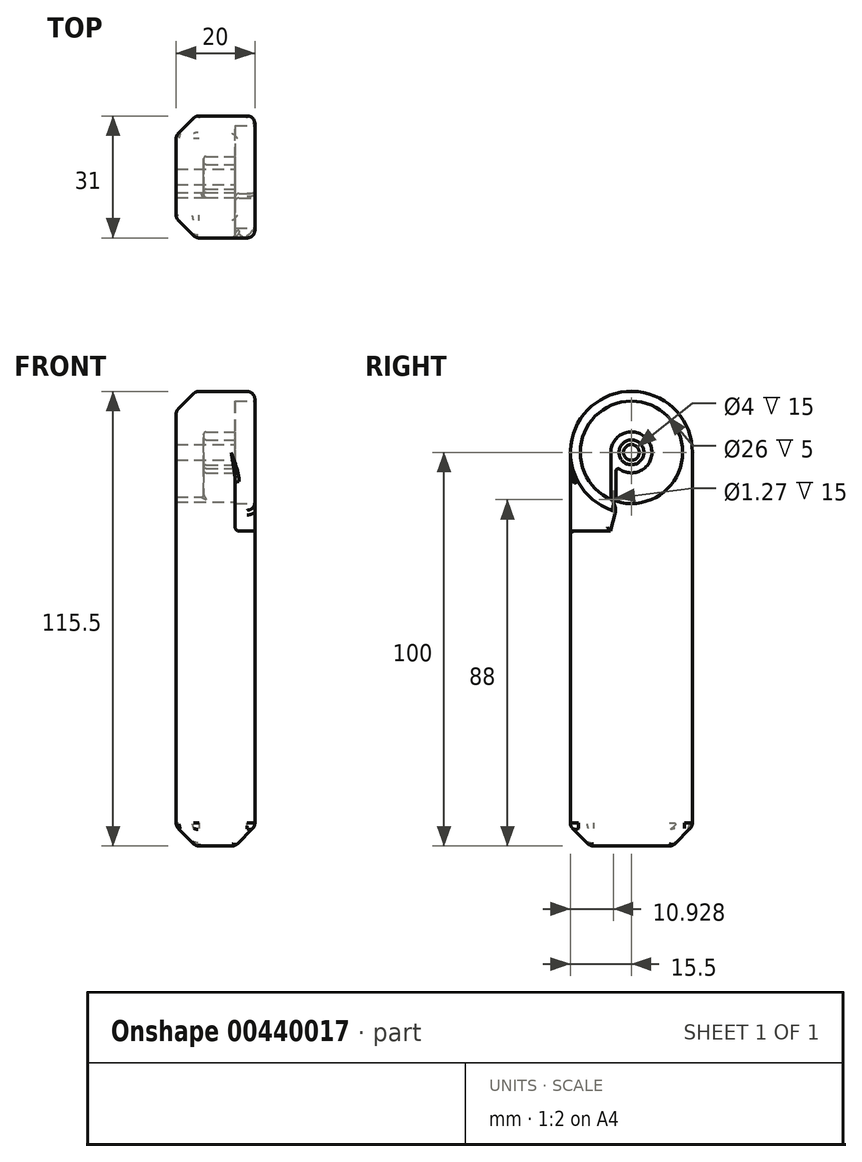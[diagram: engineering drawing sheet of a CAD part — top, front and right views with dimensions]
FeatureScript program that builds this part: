
annotation { "Feature Type Name" : "Feature", "Feature Type Description" : "" }
export const myFeature = defineFeature(function(context is Context, id is Id, definition is map)
    precondition{}
    {
        {
            var Q0;
            Q0=qCreatedBy(makeId("Right.planeOp"),FACE);
            var sketch = newSketch(context, id + "F0", { "sketchPlane" : qUnion([Q0])});
            skCircle(sketch, "E0", {"center": v(0, 0) * mm, "radius": 15.5 * mm});
            skCircle(sketch, "E1", {"center": v(0, 0) * mm, "radius": 2 * mm});
            skLineSegment(sketch, "E2.bottom", {"start": v(15.5, 0) * mm, "end": v(-15.5, 0) * mm});
            skLineSegment(sketch, "E2.top", {"start": v(15.5, -100) * mm, "end": v(-15.5, -100) * mm});
            skLineSegment(sketch, "E2.left", {"start": v(15.5, 0) * mm, "end": v(15.5, -100) * mm});
            skLineSegment(sketch, "E2.right", {"start": v(-15.5, 0) * mm, "end": v(-15.5, -100) * mm});
            skPoint(sketch, "E2.middle", {"position": v(0, -50) * mm});
            skSolve(sketch);
        }
        {
            var Q0;
            {var subQ0=sQuery(id+"F0.wireOp",EDGE,"E2.bottom");var subQ4=sQuery(id+"F0.wireOp",EDGE,"E1");var subQ5=makeQuery(id+"F0.imprint","INTERSECT",VERTEX,{"disambiguationData":[OD(0.0)],"derivedFrom":[subQ4,subQ0]});Q0=makeQuery(id+"F0.imprint","IMPRINT",FACE,{"disambiguationData":[TD([[makeQuery(id+"F0.imprint","IMPRINT",EDGE,{"disambiguationData":[TD([[subQ5,-1.0]])],"derivedFrom":subQ4}),-1.0]])]});}
            var Q1;
            {var subQ0=sQuery(id+"F0.wireOp",EDGE,"E2.bottom");var subQ4=sQuery(id+"F0.wireOp",EDGE,"E1");var subQ6=makeQuery(id+"F0.imprint","INTERSECT",VERTEX,{"disambiguationData":[OD(0.0)],"derivedFrom":[subQ4,subQ0]});Q1=makeQuery(id+"F0.imprint","IMPRINT",FACE,{"disambiguationData":[TD([[makeQuery(id+"F0.imprint","IMPRINT",EDGE,{"disambiguationData":[TD([[subQ6,1.0]])],"derivedFrom":subQ4}),-1.0]])]});}
            var Q2;
            Q2=makeQuery(id+"F0.imprint","IMPRINT",FACE,{"disambiguationData":[TD([[makeQuery(id+"F0.imprint","IMPRINT",EDGE,{"derivedFrom":sQuery(id+"F0.wireOp",EDGE,"E2.top")}),-1.0]])]});
            extrude(context, id + "F1", {"entities" : qUnion([Q0, Q1, Q2]), "oppositeDirection" : true, "depth" : 20 * mm, "offsetDistance" : 25 * mm});
        }
        {
            var Q0;
            Q0=makeQuery(id+"F1.opExtrude","CAP_FACE",FACE,{"disambiguationData":[OSD([sQuery(id+"F0.wireOp",EDGE,"E0"),sQuery(id+"F0.wireOp",EDGE,"E1"),sQuery(id+"F0.wireOp",EDGE,"E2.top"),sQuery(id+"F0.wireOp",EDGE,"E2.left"),sQuery(id+"F0.wireOp",EDGE,"E2.right")])],"isStart":true});
            var sketch = newSketch(context, id + "F2", { "sketchPlane" : qUnion([Q0])});
            skArc(sketch, "E3.0", {"start": v(15.5, 0) * mm, "mid": v(0, 15.5) * mm, "end": v(-15.5, 0) * mm});
            skCircle(sketch, "E4", {"center": v(0, 0) * mm, "radius": 15.5 * mm});
            skCircle(sketch, "E5.0", {"center": v(0, 0) * mm, "radius": 13 * mm});
            skLineSegment(sketch, "E6", {"start": v(0, 0) * mm, "end": v(-15.5, 0) * mm, "construction": true});
            skLineSegment(sketch, "E7", {"start": v(0, 0) * mm, "end": v(2.7, 15.26) * mm});
            skLineSegment(sketch, "E8", {"start": v(0, 0) * mm, "end": v(-4.01, -14.97) * mm});
            skLineSegment(sketch, "E9.0", {"start": v(-15.5, 0) * mm, "end": v(-15.5, -100) * mm});
            skLineSegment(sketch, "E10", {"start": v(-4.01, -14.97) * mm, "end": v(-5.36, -20) * mm});
            skLineSegment(sketch, "E11", {"start": v(-5.36, -20) * mm, "end": v(-15.5, -20) * mm});
            skSolve(sketch);
        }
        {
            var Q0;
            {var subQ1=sQuery(id+"F2.wireOp",EDGE,"E4");var subQ7=makeQuery(id+"F2.imprint","INTERSECT",VERTEX,{"derivedFrom":[subQ1,sQuery(id+"F2.wireOp",EDGE,"E9.0")]});Q0=makeQuery(id+"F2.imprint","IMPRINT",FACE,{"disambiguationData":[TD([[makeQuery(id+"F2.imprint","IMPRINT",EDGE,{"disambiguationData":[TD([[subQ7,1.0]])],"derivedFrom":subQ1}),1.0]])]});}
            var Q1;
            {var subQ0=sQuery(id+"F2.wireOp",EDGE,"E7");var subQ1=sQuery(id+"F2.wireOp",EDGE,"E5.0");var subQ2=makeQuery(id+"F2.imprint","INTERSECT",VERTEX,{"derivedFrom":[subQ1,subQ0]});Q1=makeQuery(id+"F2.imprint","IMPRINT",FACE,{"disambiguationData":[TD([[makeQuery(id+"F2.imprint","IMPRINT",EDGE,{"disambiguationData":[TD([[subQ2,-1.0]])],"derivedFrom":subQ1}),1.0]])]});}
            var Q2;
            {var subQ3=sQuery(id+"F2.wireOp",EDGE,"3M8qVWLi-stua-JPsy-CJId-azj3WznVmQZa");Q2=makeQuery(id+"F2.imprint","IMPRINT",FACE,{"disambiguationData":[TD([[makeQuery(id+"F2.imprint","IMPRINT",EDGE,{"derivedFrom":subQ3}),-1.0]])]});}
            var Q3;
            {var subQ0=sQuery(id+"F2.wireOp",EDGE,"E7");var subQ1=sQuery(id+"F2.wireOp",EDGE,"E5.0");var subQ2=makeQuery(id+"F2.imprint","INTERSECT",VERTEX,{"derivedFrom":[subQ1,subQ0]});Q3=makeQuery(id+"F2.imprint","IMPRINT",FACE,{"disambiguationData":[TD([[makeQuery(id+"F2.imprint","IMPRINT",EDGE,{"disambiguationData":[TD([[subQ2,1.0]])],"derivedFrom":subQ1}),1.0]])]});}
            var Q4;
            {var subQ3=sQuery(id+"F2.wireOp",EDGE,"E10");Q4=makeQuery(id+"F2.imprint","IMPRINT",FACE,{"disambiguationData":[TD([[makeQuery(id+"F2.imprint","IMPRINT",EDGE,{"derivedFrom":subQ3}),-1.0]])]});}
            extrude(context, id + "F3", {"entities" : qUnion([Q0, Q1, Q2, Q3, Q4]), "operationType" : NewBodyOperationType.REMOVE, "oppositeDirection" : true, "depth" : 5 * mm, "offsetDistance" : 25 * mm});
        }
        {
            var Q0;
            Q0=makeQuery(id+"F3.boolean.opBoolean","COPY",FACE,{"derivedFrom":makeQuery(id+"F3.opExtrude","CAP_FACE",FACE,{"disambiguationData":[OSD([sQuery(id+"F0.wireOp",EDGE,"E1"),sQuery(id+"F2.wireOp",EDGE,"E4"),sQuery(id+"F2.wireOp",EDGE,"E5.0"),sQuery(id+"F2.wireOp",EDGE,"E7"),sQuery(id+"F2.wireOp",EDGE,"E8"),sQuery(id+"F2.wireOp",EDGE,"E9.0"),sQuery(id+"F2.wireOp",EDGE,"E10"),sQuery(id+"F2.wireOp",EDGE,"E11")])],"isStart":false})});
            var sketch = newSketch(context, id + "F4", { "sketchPlane" : qUnion([Q0])});
            skCircle(sketch, "E12", {"center": v(0, 0) * mm, "radius": 3.15 * mm});
            skCircle(sketch, "E13", {"center": v(0, 0) * mm, "radius": 5.2 * mm});
            skLineSegment(sketch, "E14", {"start": v(-5.2, 0) * mm, "end": v(-5.2, -12) * mm});
            skLineSegment(sketch, "E15", {"start": v(-5.2, -12) * mm, "end": v(-3.94, -12) * mm});
            skLineSegment(sketch, "E16", {"start": v(-3.94, -12) * mm, "end": v(-3.94, -3.4) * mm});
            skCircle(sketch, "E17", {"center": v(-4.57, -12) * mm, "radius": 0.63 * mm});
            skSolve(sketch);
        }
        {
            var Q0;
            Q0=makeQuery(id+"F4.imprint","IMPRINT",FACE,{"disambiguationData":[TD([[makeQuery(id+"F4.imprint","IMPRINT",EDGE,{"derivedFrom":sQuery(id+"F4.wireOp",EDGE,"E12")}),-1.0]])]});
            var Q1;
            {var subQ0=sQuery(id+"F4.wireOp",EDGE,"E14");Q1=makeQuery(id+"F4.imprint","IMPRINT",FACE,{"disambiguationData":[TD([[makeQuery(id+"F4.imprint","IMPRINT",EDGE,{"derivedFrom":subQ0}),1.0]])]});}
            var Q2;
            {var subQ0=sQuery(id+"F4.wireOp",EDGE,"E15");Q2=makeQuery(id+"F4.imprint","IMPRINT",FACE,{"disambiguationData":[TD([[makeQuery(id+"F4.imprint","IMPRINT",EDGE,{"derivedFrom":subQ0}),-1.0]])]});}
            var Q3;
            {var subQ0=sQuery(id+"F4.wireOp",EDGE,"E15");Q3=makeQuery(id+"F4.imprint","IMPRINT",FACE,{"disambiguationData":[TD([[makeQuery(id+"F4.imprint","IMPRINT",EDGE,{"derivedFrom":subQ0}),1.0]])]});}
            extrude(context, id + "F5", {"entities" : qUnion([Q0, Q1, Q2, Q3]), "operationType" : NewBodyOperationType.REMOVE, "oppositeDirection" : true, "depth" : 8 * mm, "offsetDistance" : 25 * mm});
        }
        {
            var Q0;
            {var subQ0=sQuery(id+"F4.wireOp",EDGE,"E15");Q0=makeQuery(id+"F4.imprint","IMPRINT",FACE,{"disambiguationData":[TD([[makeQuery(id+"F4.imprint","IMPRINT",EDGE,{"derivedFrom":subQ0}),-1.0]])]});}
            var Q1;
            {var subQ0=sQuery(id+"F4.wireOp",EDGE,"E15");Q1=makeQuery(id+"F4.imprint","IMPRINT",FACE,{"disambiguationData":[TD([[makeQuery(id+"F4.imprint","IMPRINT",EDGE,{"derivedFrom":subQ0}),1.0]])]});}
            extrude(context, id + "F6", {"entities" : qUnion([Q0, Q1]), "operationType" : NewBodyOperationType.REMOVE, "endBound" : BoundingType.THROUGH_ALL, "oppositeDirection" : true, "depth" : 25 * mm, "offsetDistance" : 25 * mm});
        }
        {
            var Q0;
            Q0=makeQuery(id+"F5.boolean.opBoolean","COPY",FACE,{"derivedFrom":makeQuery(id+"F5.opExtrude","CAP_FACE",FACE,{"disambiguationData":[OSD([sQuery(id+"F4.wireOp",EDGE,"E12"),sQuery(id+"F4.wireOp",EDGE,"E13"),sQuery(id+"F4.wireOp",EDGE,"E14"),sQuery(id+"F4.wireOp",EDGE,"E16"),sQuery(id+"F4.wireOp",EDGE,"E17")])],"isStart":false})});
            var Q1;
            Q1=makeQuery(id+"F5.boolean.opBoolean","COPY",EDGE,{"derivedFrom":makeQuery(id+"F5.opExtrude","SWEPT_EDGE",EDGE,{"disambiguationData":[OSD([sQuery(id+"F4.wireOp",EDGE,"E13"),sQuery(id+"F4.wireOp",EDGE,"E16")])]})});
            var Q2;
            Q2=makeQuery(id+"F5.boolean.opBoolean","COPY",EDGE,{"derivedFrom":makeQuery(id+"F5.opExtrude","CAP_EDGE",EDGE,{"disambiguationData":[OSD([sQuery(id+"F4.wireOp",EDGE,"E13")])],"isStart":true})});
            var Q3;
            Q3=makeQuery(id+"F3.boolean.opBoolean","COPY",EDGE,{"derivedFrom":makeQuery(id+"F3.opExtrude","CAP_EDGE",EDGE,{"disambiguationData":[OSD([sQuery(id+"F0.wireOp",EDGE,"E1")])],"isStart":false})});
            fillet(context, id + "F7", {"entities" : qUnion([Q0, Q1, Q2, Q3]), "radius" : 0.6 * mm, "tangentPropagation" : true, "allowEdgeOverflow" : false});
        }
        {
            var Q0;
            Q0=makeQuery(id+"F1.opExtrude","CAP_EDGE",EDGE,{"disambiguationData":[OSD([sQuery(id+"F0.wireOp",EDGE,"E0")])],"isStart":false});
            var Q1;
            Q1=makeQuery(id+"F1.opExtrude","CAP_EDGE",EDGE,{"disambiguationData":[OSD([sQuery(id+"F0.wireOp",EDGE,"E2.top")])],"isStart":false});
            var Q2;
            Q2=makeQuery(id+"F1.opExtrude","SWEPT_EDGE",EDGE,{"disambiguationData":[OSD([sQuery(id+"F0.wireOp",EDGE,"E2.top"),sQuery(id+"F0.wireOp",EDGE,"E2.right")])]});
            var Q3;
            Q3=makeQuery(id+"F1.opExtrude","SWEPT_EDGE",EDGE,{"disambiguationData":[OSD([sQuery(id+"F0.wireOp",EDGE,"E2.top"),sQuery(id+"F0.wireOp",EDGE,"E2.left")])]});
            var Q4;
            Q4=makeQuery(id+"F1.opExtrude","CAP_EDGE",EDGE,{"disambiguationData":[OSD([sQuery(id+"F0.wireOp",EDGE,"E2.top")])],"isStart":true});
            chamfer(context, id + "F8", {"entities" : qUnion([Q0, Q1, Q2, Q3, Q4]), "width" : 5 * mm, "tangentPropagation" : true});
        }
        {
            var Q0;
            {var subQ0=sQuery(id+"F0.wireOp",EDGE,"E2.right");Q0=makeQuery(id+"F8.opChamfer","BLEND_EDGE",EDGE,{"blendedFrom":[makeQuery(id+"F1.opExtrude","CAP_EDGE",EDGE,{"disambiguationData":[OSD([subQ0])],"isStart":false}),makeQuery(id+"F1.opExtrude","CAP_FACE",FACE,{"disambiguationData":[OSD([sQuery(id+"F0.wireOp",EDGE,"E0"),sQuery(id+"F0.wireOp",EDGE,"E1"),sQuery(id+"F0.wireOp",EDGE,"E2.top"),sQuery(id+"F0.wireOp",EDGE,"E2.left"),subQ0])],"isStart":false})],"blendedInto":[makeQuery(id+"F1.opExtrude","CAP_FACE",FACE,{"disambiguationData":[OSD([sQuery(id+"F0.wireOp",EDGE,"E0"),sQuery(id+"F0.wireOp",EDGE,"E1"),sQuery(id+"F0.wireOp",EDGE,"E2.top"),sQuery(id+"F0.wireOp",EDGE,"E2.left"),subQ0])],"isStart":false})]});}
            var Q1;
            {var subQ0=sQuery(id+"F0.wireOp",EDGE,"E2.top");Q1=makeQuery(id+"F8.opChamfer","BLEND_EDGE",EDGE,{"blendedFrom":[makeQuery(id+"F1.opExtrude","CAP_EDGE",EDGE,{"disambiguationData":[OSD([subQ0])],"isStart":false}),makeQuery(id+"F1.opExtrude","CAP_FACE",FACE,{"disambiguationData":[OSD([sQuery(id+"F0.wireOp",EDGE,"E0"),sQuery(id+"F0.wireOp",EDGE,"E1"),subQ0,sQuery(id+"F0.wireOp",EDGE,"E2.left"),sQuery(id+"F0.wireOp",EDGE,"E2.right")])],"isStart":false})],"blendedInto":[makeQuery(id+"F1.opExtrude","CAP_FACE",FACE,{"disambiguationData":[OSD([sQuery(id+"F0.wireOp",EDGE,"E0"),sQuery(id+"F0.wireOp",EDGE,"E1"),subQ0,sQuery(id+"F0.wireOp",EDGE,"E2.left"),sQuery(id+"F0.wireOp",EDGE,"E2.right")])],"isStart":false})]});}
            var Q2;
            {var subQ0=sQuery(id+"F0.wireOp",EDGE,"E2.right");var subQ1=sQuery(id+"F0.wireOp",EDGE,"E2.top");Q2=makeQuery(id+"F8.opChamfer","BLEND_EDGE",EDGE,{"blendedFrom":[makeQuery(id+"F1.opExtrude","CAP_VERTEX",VERTEX,{"disambiguationData":[OSD([subQ1,subQ0])],"isStart":false}),makeQuery(id+"F1.opExtrude","SWEPT_EDGE",EDGE,{"disambiguationData":[OSD([subQ1,subQ0])]})],"blendedInto":[]});}
            var Q3;
            {var subQ0=sQuery(id+"F0.wireOp",EDGE,"E2.right");var subQ1=sQuery(id+"F0.wireOp",EDGE,"E2.top");Q3=makeQuery(id+"F8.opChamfer","BLEND_FACE",FACE,{"disambiguationData":[OSD([subQ1,subQ0]),TDD([makeQuery(id+"F1.opExtrude","CAP_VERTEX",VERTEX,{"disambiguationData":[OSD([subQ1,subQ0])],"isStart":false})])]});}
            var Q4;
            {var subQ0=sQuery(id+"F0.wireOp",EDGE,"E2.top");Q4=makeQuery(id+"F8.opChamfer","BLEND_EDGE",EDGE,{"blendedFrom":[makeQuery(id+"F1.opExtrude","CAP_EDGE",EDGE,{"disambiguationData":[OSD([subQ0])],"isStart":false}),makeQuery(id+"F1.opExtrude","SWEPT_FACE",FACE,{"disambiguationData":[OSD([subQ0])]})],"blendedInto":[makeQuery(id+"F1.opExtrude","SWEPT_FACE",FACE,{"disambiguationData":[OSD([subQ0])]})]});}
            var Q5;
            {var subQ0=sQuery(id+"F0.wireOp",EDGE,"E2.top");Q5=makeQuery(id+"F8.opChamfer","BLEND_EDGE",EDGE,{"blendedFrom":[makeQuery(id+"F1.opExtrude","SWEPT_EDGE",EDGE,{"disambiguationData":[OSD([subQ0,sQuery(id+"F0.wireOp",EDGE,"E2.right")])]}),makeQuery(id+"F1.opExtrude","SWEPT_FACE",FACE,{"disambiguationData":[OSD([subQ0])]})],"blendedInto":[makeQuery(id+"F1.opExtrude","SWEPT_FACE",FACE,{"disambiguationData":[OSD([subQ0])]})]});}
            var Q6;
            {var subQ0=sQuery(id+"F0.wireOp",EDGE,"E2.right");Q6=makeQuery(id+"F8.opChamfer","BLEND_EDGE",EDGE,{"blendedFrom":[makeQuery(id+"F1.opExtrude","SWEPT_EDGE",EDGE,{"disambiguationData":[OSD([sQuery(id+"F0.wireOp",EDGE,"E2.top"),subQ0])]}),makeQuery(id+"F1.opExtrude","SWEPT_FACE",FACE,{"disambiguationData":[OSD([subQ0])]})],"blendedInto":[makeQuery(id+"F1.opExtrude","SWEPT_FACE",FACE,{"disambiguationData":[OSD([subQ0])]})]});}
            var Q7;
            {var subQ0=sQuery(id+"F0.wireOp",EDGE,"E2.right");Q7=makeQuery(id+"F8.opChamfer","BLEND_EDGE",EDGE,{"blendedFrom":[makeQuery(id+"F1.opExtrude","CAP_EDGE",EDGE,{"disambiguationData":[OSD([subQ0])],"isStart":false}),makeQuery(id+"F1.opExtrude","SWEPT_FACE",FACE,{"disambiguationData":[OSD([subQ0])]})],"blendedInto":[makeQuery(id+"F1.opExtrude","SWEPT_FACE",FACE,{"disambiguationData":[OSD([subQ0])]})]});}
            var Q8;
            {var subQ0=sQuery(id+"F0.wireOp",EDGE,"E2.top");Q8=makeQuery(id+"F8.opChamfer","BLEND_EDGE",EDGE,{"blendedFrom":[makeQuery(id+"F1.opExtrude","CAP_VERTEX",VERTEX,{"disambiguationData":[OSD([subQ0,sQuery(id+"F0.wireOp",EDGE,"E2.left")])],"isStart":false}),makeQuery(id+"F1.opExtrude","CAP_EDGE",EDGE,{"disambiguationData":[OSD([subQ0])],"isStart":false})],"blendedInto":[]});}
            var Q9;
            {var subQ0=sQuery(id+"F0.wireOp",EDGE,"E2.left");Q9=makeQuery(id+"F8.opChamfer","BLEND_EDGE",EDGE,{"blendedFrom":[makeQuery(id+"F1.opExtrude","CAP_VERTEX",VERTEX,{"disambiguationData":[OSD([sQuery(id+"F0.wireOp",EDGE,"E2.top"),subQ0])],"isStart":false}),makeQuery(id+"F1.opExtrude","CAP_EDGE",EDGE,{"disambiguationData":[OSD([subQ0])],"isStart":false})],"blendedInto":[]});}
            var Q10;
            {var subQ0=sQuery(id+"F0.wireOp",EDGE,"E2.left");var subQ1=sQuery(id+"F0.wireOp",EDGE,"E2.top");Q10=makeQuery(id+"F8.opChamfer","BLEND_EDGE",EDGE,{"blendedFrom":[makeQuery(id+"F1.opExtrude","CAP_VERTEX",VERTEX,{"disambiguationData":[OSD([subQ1,subQ0])],"isStart":false}),makeQuery(id+"F1.opExtrude","SWEPT_EDGE",EDGE,{"disambiguationData":[OSD([subQ1,subQ0])]})],"blendedInto":[]});}
            var Q11;
            {var subQ0=sQuery(id+"F0.wireOp",EDGE,"E2.left");Q11=makeQuery(id+"F8.opChamfer","BLEND_EDGE",EDGE,{"blendedFrom":[makeQuery(id+"F1.opExtrude","SWEPT_EDGE",EDGE,{"disambiguationData":[OSD([sQuery(id+"F0.wireOp",EDGE,"E2.top"),subQ0])]}),makeQuery(id+"F1.opExtrude","SWEPT_FACE",FACE,{"disambiguationData":[OSD([subQ0])]})],"blendedInto":[makeQuery(id+"F1.opExtrude","SWEPT_FACE",FACE,{"disambiguationData":[OSD([subQ0])]})]});}
            var Q12;
            {var subQ0=sQuery(id+"F0.wireOp",EDGE,"E2.top");Q12=makeQuery(id+"F8.opChamfer","BLEND_EDGE",EDGE,{"blendedFrom":[makeQuery(id+"F1.opExtrude","SWEPT_EDGE",EDGE,{"disambiguationData":[OSD([subQ0,sQuery(id+"F0.wireOp",EDGE,"E2.left")])]}),makeQuery(id+"F1.opExtrude","SWEPT_FACE",FACE,{"disambiguationData":[OSD([subQ0])]})],"blendedInto":[makeQuery(id+"F1.opExtrude","SWEPT_FACE",FACE,{"disambiguationData":[OSD([subQ0])]})]});}
            var Q13;
            {var subQ0=sQuery(id+"F0.wireOp",EDGE,"E2.top");Q13=makeQuery(id+"F8.opChamfer","BLEND_EDGE",EDGE,{"blendedFrom":[makeQuery(id+"F1.opExtrude","SWEPT_EDGE",EDGE,{"disambiguationData":[OSD([subQ0,sQuery(id+"F0.wireOp",EDGE,"E2.right")])]}),makeQuery(id+"F1.opExtrude","CAP_EDGE",EDGE,{"disambiguationData":[OSD([subQ0])],"isStart":true})],"blendedInto":[]});}
            var Q14;
            {var subQ0=sQuery(id+"F0.wireOp",EDGE,"E2.top");Q14=makeQuery(id+"F8.opChamfer","BLEND_EDGE",EDGE,{"blendedFrom":[makeQuery(id+"F1.opExtrude","CAP_EDGE",EDGE,{"disambiguationData":[OSD([subQ0])],"isStart":true}),makeQuery(id+"F1.opExtrude","SWEPT_FACE",FACE,{"disambiguationData":[OSD([subQ0])]})],"blendedInto":[makeQuery(id+"F1.opExtrude","SWEPT_FACE",FACE,{"disambiguationData":[OSD([subQ0])]})]});}
            var Q15;
            {var subQ0=sQuery(id+"F0.wireOp",EDGE,"E2.top");Q15=makeQuery(id+"F8.opChamfer","BLEND_EDGE",EDGE,{"blendedFrom":[makeQuery(id+"F1.opExtrude","CAP_EDGE",EDGE,{"disambiguationData":[OSD([subQ0])],"isStart":true}),makeQuery(id+"F1.opExtrude","CAP_FACE",FACE,{"disambiguationData":[OSD([sQuery(id+"F0.wireOp",EDGE,"E0"),sQuery(id+"F0.wireOp",EDGE,"E1"),subQ0,sQuery(id+"F0.wireOp",EDGE,"E2.left"),sQuery(id+"F0.wireOp",EDGE,"E2.right")])],"isStart":true})],"blendedInto":[makeQuery(id+"F1.opExtrude","CAP_FACE",FACE,{"disambiguationData":[OSD([sQuery(id+"F0.wireOp",EDGE,"E0"),sQuery(id+"F0.wireOp",EDGE,"E1"),subQ0,sQuery(id+"F0.wireOp",EDGE,"E2.left"),sQuery(id+"F0.wireOp",EDGE,"E2.right")])],"isStart":true})]});}
            var Q16;
            {var subQ0=sQuery(id+"F0.wireOp",EDGE,"E2.top");Q16=makeQuery(id+"F8.opChamfer","BLEND_EDGE",EDGE,{"blendedFrom":[makeQuery(id+"F1.opExtrude","SWEPT_EDGE",EDGE,{"disambiguationData":[OSD([subQ0,sQuery(id+"F0.wireOp",EDGE,"E2.left")])]}),makeQuery(id+"F1.opExtrude","CAP_EDGE",EDGE,{"disambiguationData":[OSD([subQ0])],"isStart":true})],"blendedInto":[]});}
            var Q17;
            Q17=makeQuery(id+"F1.opExtrude","CAP_EDGE",EDGE,{"disambiguationData":[OSD([sQuery(id+"F0.wireOp",EDGE,"E2.left")])],"isStart":true});
            var Q18;
            Q18=makeQuery(id+"F1.opExtrude","CAP_EDGE",EDGE,{"disambiguationData":[OSD([sQuery(id+"F0.wireOp",EDGE,"E2.right")])],"isStart":true});
            fillet(context, id + "F9", {"entities" : qUnion([Q0, Q1, Q2, Q3, Q4, Q5, Q6, Q7, Q8, Q9, Q10, Q11, Q12, Q13, Q14, Q15, Q16, Q17, Q18]), "radius" : 2 * mm, "tangentPropagation" : true, "allowEdgeOverflow" : false});
        }
        {
            var Q0;
            {var subQ0=sQuery(id+"F2.wireOp",EDGE,"E7");var subQ1=sQuery(id+"F2.wireOp",EDGE,"E5.0");var subQ2=sQuery(id+"F2.wireOp",EDGE,"E10");var subQ3=sQuery(id+"F2.wireOp",EDGE,"E8");var subQ4=sQuery(id+"F2.wireOp",EDGE,"E11");Q0=makeQuery(id+"F5.boolean.opBoolean","SPLIT",FACE,{"disambiguationData":[TD([makeQuery(id+"F1.opExtrude","SWEPT_FACE",FACE,{"disambiguationData":[OSD([sQuery(id+"F0.wireOp",EDGE,"E0")])]})])],"derivedFrom":makeQuery(id+"F3.boolean.opBoolean","COPY",FACE,{"derivedFrom":makeQuery(id+"F3.opExtrude","CAP_FACE",FACE,{"disambiguationData":[OSD([sQuery(id+"F0.wireOp",EDGE,"E1"),sQuery(id+"F2.wireOp",EDGE,"E4"),subQ1,subQ0,subQ3,sQuery(id+"F2.wireOp",EDGE,"E9.0"),subQ2,subQ4])],"isStart":false})})});}
            var Q1;
            Q1=makeQuery(id+"F3.boolean.opBoolean","COPY",EDGE,{"derivedFrom":makeQuery(id+"F3.opExtrude","SWEPT_EDGE",EDGE,{"disambiguationData":[OSD([sQuery(id+"F2.wireOp",EDGE,"E5.0"),sQuery(id+"F2.wireOp",EDGE,"E8")])]})});
            var Q2;
            Q2=makeQuery(id+"F3.boolean.opBoolean","COPY",EDGE,{"derivedFrom":makeQuery(id+"F3.opExtrude","CAP_EDGE",EDGE,{"disambiguationData":[OSD([sQuery(id+"F2.wireOp",EDGE,"E8"),sQuery(id+"F2.wireOp",EDGE,"E10")])],"isStart":true})});
            fillet(context, id + "F10", {"entities" : qUnion([Q0, Q1, Q2]), "radius" : 1 * mm, "tangentPropagation" : true, "allowEdgeOverflow" : false});
        }
    });
